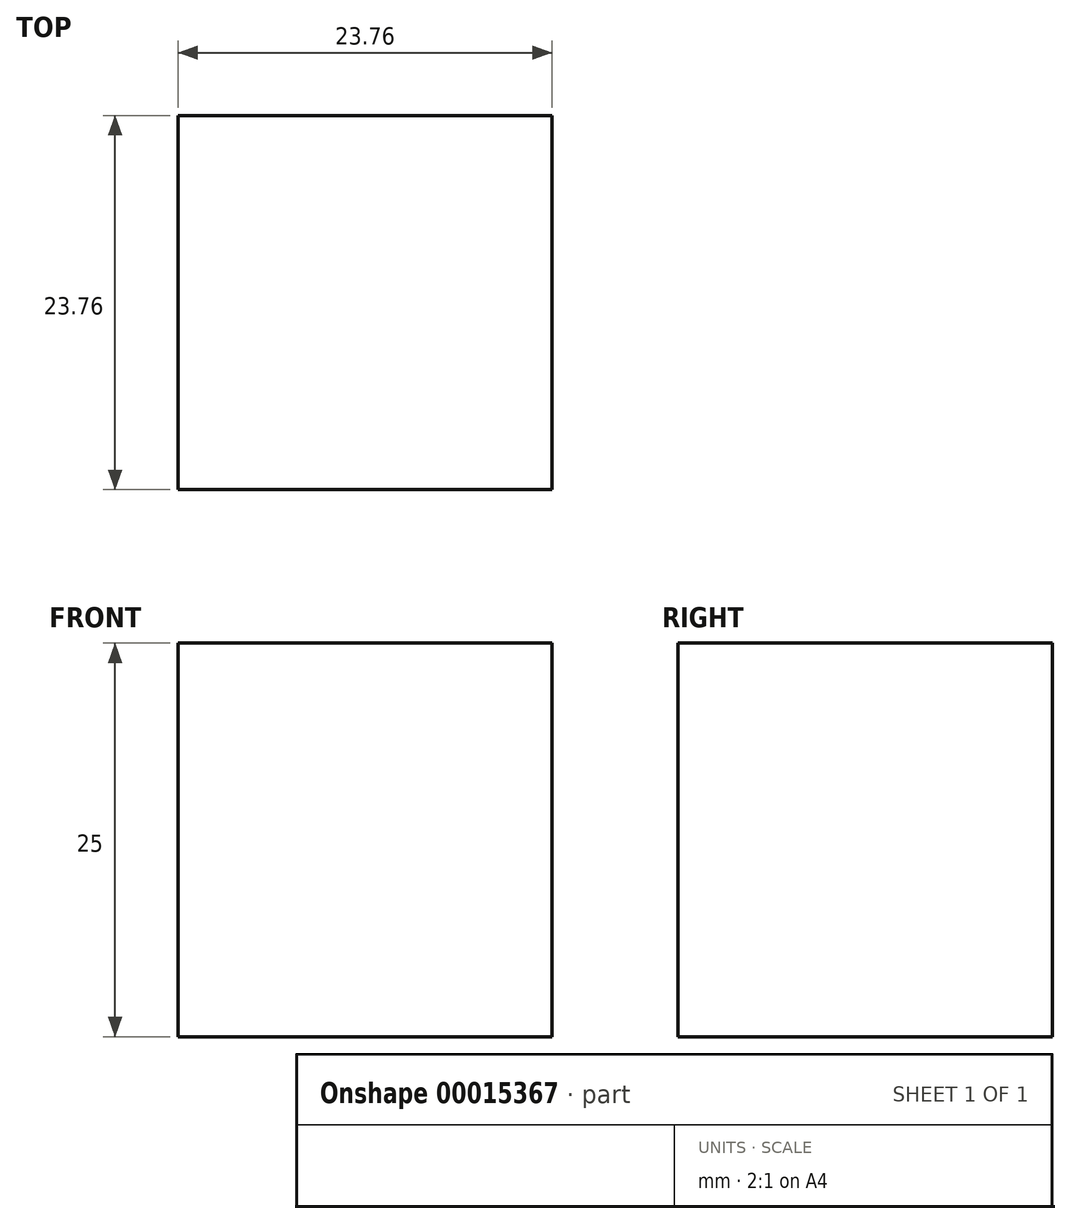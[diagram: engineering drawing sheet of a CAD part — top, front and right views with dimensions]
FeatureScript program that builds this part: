
annotation { "Feature Type Name" : "Feature", "Feature Type Description" : "" }
export const myFeature = defineFeature(function(context is Context, id is Id, definition is map)
    precondition{}
    {
        {
            var Q0;
            Q0=qCreatedBy(makeId("Top.planeOp"),FACE);
            var sketch = newSketch(context, id + "F0", { "sketchPlane" : qUnion([Q0])});
            skLineSegment(sketch, "E0.bottom", {"start": v(0, 0) * mm, "end": v(23.76, 0) * mm});
            skLineSegment(sketch, "E0.top", {"start": v(0, 23.76) * mm, "end": v(23.76, 23.76) * mm});
            skLineSegment(sketch, "E0.left", {"start": v(0, 0) * mm, "end": v(0, 23.76) * mm});
            skLineSegment(sketch, "E0.right", {"start": v(23.76, 0) * mm, "end": v(23.76, 23.76) * mm});
            skSolve(sketch);
        }
        {
            var Q0;
            Q0=makeQuery(id+"F0.imprint","IMPRINT",FACE,{"disambiguationData":[TD([[makeQuery(id+"F0.imprint","IMPRINT",EDGE,{"derivedFrom":sQuery(id+"F0.wireOp",EDGE,"E0.bottom")}),1.0]])]});
            extrude(context, id + "F1", {"entities" : qUnion([Q0]), "depth" : 25 * mm});
        }
    });
